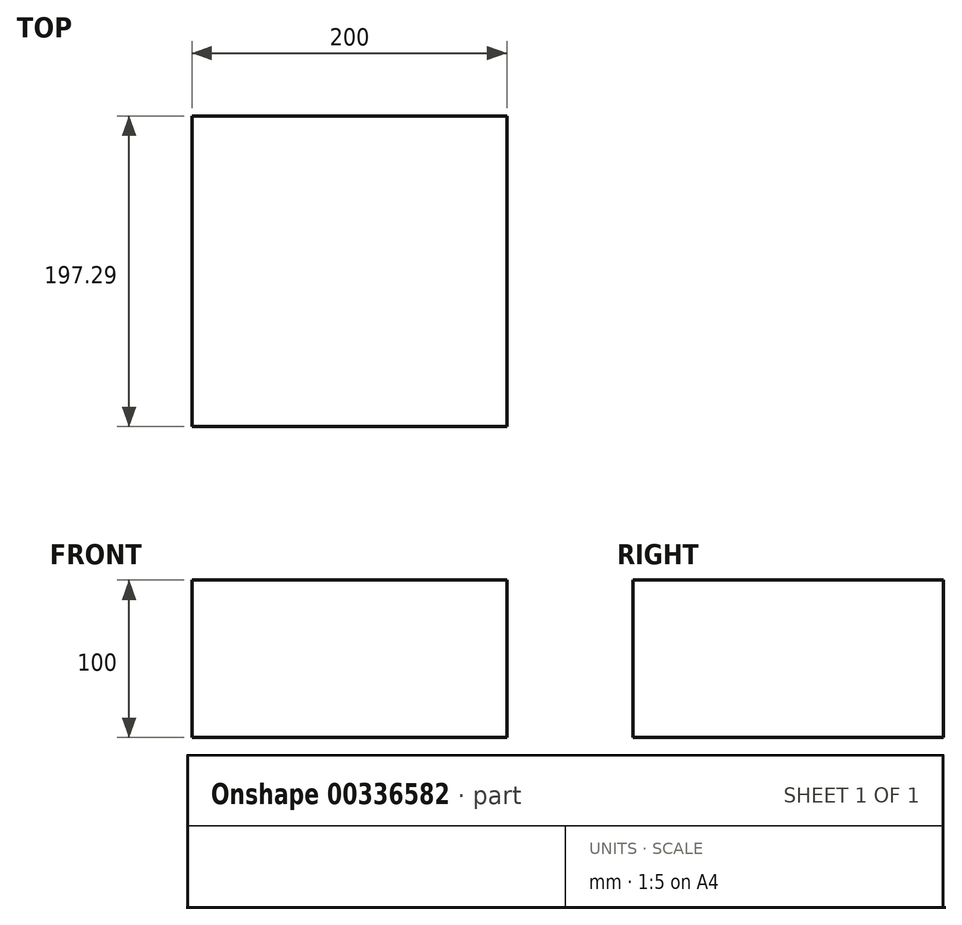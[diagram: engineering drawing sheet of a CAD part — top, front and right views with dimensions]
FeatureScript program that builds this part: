
annotation { "Feature Type Name" : "Feature", "Feature Type Description" : "" }
export const myFeature = defineFeature(function(context is Context, id is Id, definition is map)
    precondition{}
    {
        {
            var Q0;
            Q0=qCreatedBy(makeId("Right.planeOp"),FACE);
            var sketch = newSketch(context, id + "F0", { "sketchPlane" : qUnion([Q0])});
            skLineSegment(sketch, "E0.bottom", {"start": v(-93.82, 55.6) * mm, "end": v(103.47, 55.6) * mm});
            skLineSegment(sketch, "E0.top", {"start": v(-93.82, -44.4) * mm, "end": v(103.47, -44.4) * mm});
            skLineSegment(sketch, "E0.left", {"start": v(-93.82, 55.6) * mm, "end": v(-93.82, -44.4) * mm});
            skLineSegment(sketch, "E0.right", {"start": v(103.47, 55.6) * mm, "end": v(103.47, -44.4) * mm});
            skSolve(sketch);
        }
        {
            var Q0;
            Q0 = qSketchRegion(id + "F0", true);
            extrude(context, id + "F1", {"entities" : qUnion([Q0]), "depth" : 200 * mm});
        }
    });
